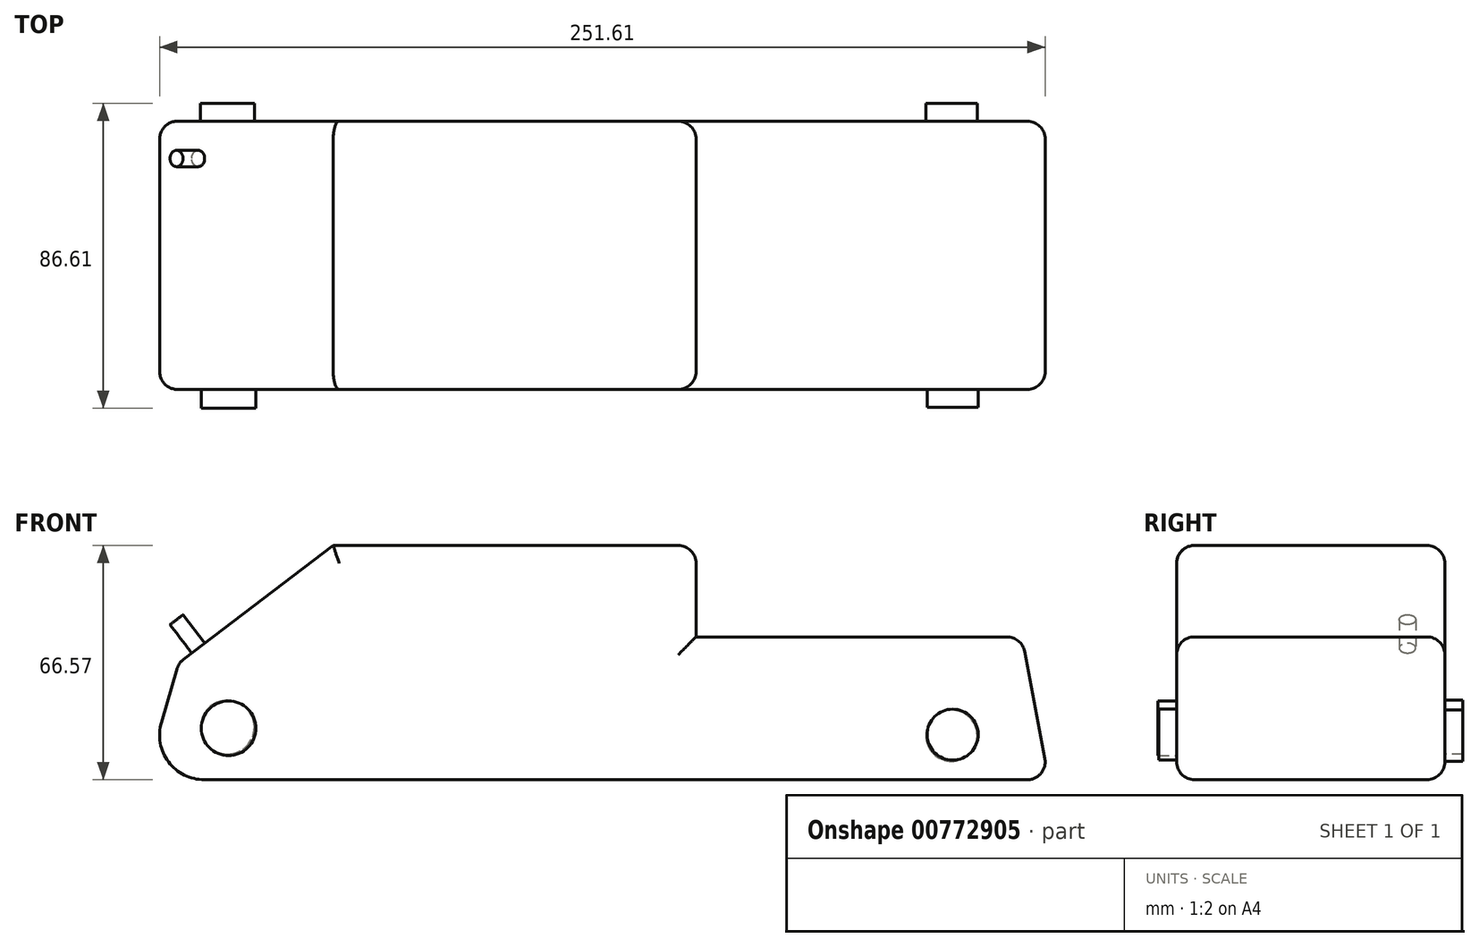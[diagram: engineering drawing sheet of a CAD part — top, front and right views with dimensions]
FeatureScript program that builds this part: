
annotation { "Feature Type Name" : "Feature", "Feature Type Description" : "" }
export const myFeature = defineFeature(function(context is Context, id is Id, definition is map)
    precondition{}
    {
        {
            var Q0;
            Q0=qCreatedBy(makeId("Front.planeOp"),FACE);
            var sketch = newSketch(context, id + "F0", { "sketchPlane" : qUnion([Q0])});
            skLineSegment(sketch, "E0", {"start": v(-130.55, -33.23) * mm, "end": v(126.37, -33.23) * mm});
            skLineSegment(sketch, "E1", {"start": v(126.37, -33.23) * mm, "end": v(118.66, 7.36) * mm});
            skLineSegment(sketch, "E2", {"start": v(118.66, 7.36) * mm, "end": v(26.12, 7.36) * mm});
            skLineSegment(sketch, "E3", {"start": v(26.12, 7.36) * mm, "end": v(26.12, 33.34) * mm});
            skLineSegment(sketch, "E4", {"start": v(26.12, 33.34) * mm, "end": v(-76.97, 33.34) * mm});
            skLineSegment(sketch, "E5", {"start": v(-76.97, 33.34) * mm, "end": v(-120.8, 0) * mm});
            skLineSegment(sketch, "E6", {"start": v(-120.8, 0) * mm, "end": v(-130.55, -33.23) * mm});
            skSolve(sketch);
        }
        {
            var Q0;
            Q0=makeQuery(id+"F0.imprint","IMPRINT",FACE,{"disambiguationData":[TD([[makeQuery(id+"F0.imprint","IMPRINT",EDGE,{"derivedFrom":sQuery(id+"F0.wireOp",EDGE,"E0")}),1.0]])]});
            extrude(context, id + "F1", {"entities" : qUnion([Q0]), "depth" : 76.2 * mm, "offsetDistance" : 25.4 * mm});
        }
        {
            var Q0;
            Q0=makeQuery(id+"F1.opExtrude","CAP_EDGE",EDGE,{"disambiguationData":[OSD([sQuery(id+"F0.wireOp",EDGE,"E6")])],"isStart":false});
            var Q1;
            Q1=makeQuery(id+"F1.opExtrude","CAP_EDGE",EDGE,{"disambiguationData":[OSD([sQuery(id+"F0.wireOp",EDGE,"E5")])],"isStart":false});
            var Q2;
            Q2=makeQuery(id+"F1.opExtrude","CAP_EDGE",EDGE,{"disambiguationData":[OSD([sQuery(id+"F0.wireOp",EDGE,"E4")])],"isStart":false});
            var Q3;
            Q3=makeQuery(id+"F1.opExtrude","CAP_EDGE",EDGE,{"disambiguationData":[OSD([sQuery(id+"F0.wireOp",EDGE,"E3")])],"isStart":false});
            var Q4;
            Q4=makeQuery(id+"F1.opExtrude","CAP_EDGE",EDGE,{"disambiguationData":[OSD([sQuery(id+"F0.wireOp",EDGE,"E3")])],"isStart":true});
            var Q5;
            Q5=makeQuery(id+"F1.opExtrude","SWEPT_EDGE",EDGE,{"disambiguationData":[OSD([sQuery(id+"F0.wireOp",EDGE,"E3"),sQuery(id+"F0.wireOp",EDGE,"E4")])]});
            var Q6;
            Q6=makeQuery(id+"F1.opExtrude","CAP_EDGE",EDGE,{"disambiguationData":[OSD([sQuery(id+"F0.wireOp",EDGE,"E5")])],"isStart":true});
            var Q7;
            Q7=makeQuery(id+"F1.opExtrude","CAP_EDGE",EDGE,{"disambiguationData":[OSD([sQuery(id+"F0.wireOp",EDGE,"E4")])],"isStart":true});
            var Q8;
            Q8=makeQuery(id+"F1.opExtrude","CAP_EDGE",EDGE,{"disambiguationData":[OSD([sQuery(id+"F0.wireOp",EDGE,"E6")])],"isStart":true});
            var Q9;
            Q9=makeQuery(id+"F1.opExtrude","CAP_EDGE",EDGE,{"disambiguationData":[OSD([sQuery(id+"F0.wireOp",EDGE,"E0")])],"isStart":true});
            var Q10;
            Q10=makeQuery(id+"F1.opExtrude","SWEPT_EDGE",EDGE,{"disambiguationData":[OSD([sQuery(id+"F0.wireOp",EDGE,"E5"),sQuery(id+"F0.wireOp",EDGE,"E6")])]});
            var Q11;
            Q11=makeQuery(id+"F1.opExtrude","CAP_EDGE",EDGE,{"disambiguationData":[OSD([sQuery(id+"F0.wireOp",EDGE,"E0")])],"isStart":false});
            var Q12;
            Q12=makeQuery(id+"F1.opExtrude","CAP_EDGE",EDGE,{"disambiguationData":[OSD([sQuery(id+"F0.wireOp",EDGE,"E2")])],"isStart":false});
            var Q13;
            Q13=makeQuery(id+"F1.opExtrude","SWEPT_EDGE",EDGE,{"disambiguationData":[OSD([sQuery(id+"F0.wireOp",EDGE,"E1"),sQuery(id+"F0.wireOp",EDGE,"E2")])]});
            var Q14;
            Q14=makeQuery(id+"F1.opExtrude","CAP_EDGE",EDGE,{"disambiguationData":[OSD([sQuery(id+"F0.wireOp",EDGE,"E1")])],"isStart":false});
            var Q15;
            Q15=makeQuery(id+"F1.opExtrude","SWEPT_EDGE",EDGE,{"disambiguationData":[OSD([sQuery(id+"F0.wireOp",EDGE,"E0"),sQuery(id+"F0.wireOp",EDGE,"E1")])]});
            var Q16;
            Q16=makeQuery(id+"F1.opExtrude","CAP_EDGE",EDGE,{"disambiguationData":[OSD([sQuery(id+"F0.wireOp",EDGE,"E1")])],"isStart":true});
            var Q17;
            Q17=makeQuery(id+"F1.opExtrude","CAP_EDGE",EDGE,{"disambiguationData":[OSD([sQuery(id+"F0.wireOp",EDGE,"E2")])],"isStart":true});
            fillet(context, id + "F2", {"entities" : qUnion([Q0, Q1, Q2, Q3, Q4, Q5, Q6, Q7, Q8, Q9, Q10, Q11, Q12, Q13, Q14, Q15, Q16, Q17]), "radius" : 5.08 * mm, "tangentPropagation" : true, "allowEdgeOverflow" : false});
        }
        {
            var Q0;
            Q0=makeQuery(id+"F1.opExtrude","SWEPT_EDGE",EDGE,{"disambiguationData":[OSD([sQuery(id+"F0.wireOp",EDGE,"E0"),sQuery(id+"F0.wireOp",EDGE,"E6")])]});
            fillet(context, id + "F3", {"entities" : qUnion([Q0]), "radius" : 12.7 * mm, "tangentPropagation" : true, "allowEdgeOverflow" : false});
        }
        {
            var Q0;
            Q0=makeQuery(id+"F1.opExtrude","CAP_FACE",FACE,{"disambiguationData":[OSD([sQuery(id+"F0.wireOp",EDGE,"E0"),sQuery(id+"F0.wireOp",EDGE,"E1"),sQuery(id+"F0.wireOp",EDGE,"E2"),sQuery(id+"F0.wireOp",EDGE,"E3"),sQuery(id+"F0.wireOp",EDGE,"E4"),sQuery(id+"F0.wireOp",EDGE,"E5"),sQuery(id+"F0.wireOp",EDGE,"E6")])],"isStart":false});
            var sketch = newSketch(context, id + "F4", { "sketchPlane" : qUnion([Q0])});
            skCircle(sketch, "E7", {"center": v(-106.68, -18.61) * mm, "radius": 7.75 * mm});
            skSolve(sketch);
        }
        {
            var Q0;
            Q0=makeQuery(id+"F4.imprint","IMPRINT",FACE,{"disambiguationData":[TD([[makeQuery(id+"F4.imprint","IMPRINT",EDGE,{"derivedFrom":sQuery(id+"F4.wireOp",EDGE,"E7")}),1.0]])]});
            extrude(context, id + "F5", {"entities" : qUnion([Q0]), "operationType" : NewBodyOperationType.ADD, "depth" : 0.25 * mm, "offsetDistance" : 25.4 * mm});
        }
        {
            var Q0;
            Q0=makeQuery(id+"F5.opExtrude","CAP_FACE",FACE,{"disambiguationData":[OSD([sQuery(id+"F4.wireOp",EDGE,"E7")])],"isStart":false});
            extrude(context, id + "F6", {"entities" : qUnion([Q0]), "operationType" : NewBodyOperationType.ADD, "depth" : 5.08 * mm, "offsetDistance" : 25.4 * mm});
        }
        {
            var Q0;
            Q0=makeQuery(id+"F1.opExtrude","CAP_FACE",FACE,{"disambiguationData":[OSD([sQuery(id+"F0.wireOp",EDGE,"E0"),sQuery(id+"F0.wireOp",EDGE,"E1"),sQuery(id+"F0.wireOp",EDGE,"E2"),sQuery(id+"F0.wireOp",EDGE,"E3"),sQuery(id+"F0.wireOp",EDGE,"E4"),sQuery(id+"F0.wireOp",EDGE,"E5"),sQuery(id+"F0.wireOp",EDGE,"E6")])],"isStart":true});
            var sketch = newSketch(context, id + "F7", { "sketchPlane" : qUnion([Q0])});
            skCircle(sketch, "E8", {"center": v(107.01, -18.29) * mm, "radius": 7.64 * mm});
            skSolve(sketch);
        }
        {
            var Q0;
            Q0=makeQuery(id+"F7.imprint","IMPRINT",FACE,{"disambiguationData":[TD([[makeQuery(id+"F7.imprint","IMPRINT",EDGE,{"derivedFrom":sQuery(id+"F7.wireOp",EDGE,"E8")}),1.0]])]});
            extrude(context, id + "F8", {"entities" : qUnion([Q0]), "operationType" : NewBodyOperationType.ADD, "depth" : 5.08 * mm, "offsetDistance" : 25.4 * mm});
        }
        {
            var Q0;
            Q0=makeQuery(id+"F4.imprint","IMPRINT",FACE,{"disambiguationData":[TD([[makeQuery(id+"F4.imprint","IMPRINT",EDGE,{"derivedFrom":sQuery(id+"F4.wireOp",EDGE,"E7")}),-1.0]])]});
            var sketch = newSketch(context, id + "F9", { "sketchPlane" : qUnion([Q0])});
            skCircle(sketch, "E9", {"center": v(99.03, -20.42) * mm, "radius": 7.25 * mm});
            skSolve(sketch);
        }
        {
            var Q0;
            Q0=makeQuery(id+"F1.opExtrude","CAP_FACE",FACE,{"disambiguationData":[OSD([sQuery(id+"F0.wireOp",EDGE,"E0"),sQuery(id+"F0.wireOp",EDGE,"E1"),sQuery(id+"F0.wireOp",EDGE,"E2"),sQuery(id+"F0.wireOp",EDGE,"E3"),sQuery(id+"F0.wireOp",EDGE,"E4"),sQuery(id+"F0.wireOp",EDGE,"E5"),sQuery(id+"F0.wireOp",EDGE,"E6")])],"isStart":true});
            var sketch = newSketch(context, id + "F10", { "sketchPlane" : qUnion([Q0])});
            skCircle(sketch, "E10", {"center": v(-98.73, -20.73) * mm, "radius": 7.27 * mm});
            skSolve(sketch);
        }
        {
            var Q0;
            Q0=makeQuery(id+"F10.imprint","IMPRINT",FACE,{"disambiguationData":[TD([[makeQuery(id+"F10.imprint","IMPRINT",EDGE,{"derivedFrom":sQuery(id+"F10.wireOp",EDGE,"E10")}),1.0]])]});
            extrude(context, id + "F11", {"entities" : qUnion([Q0]), "operationType" : NewBodyOperationType.ADD, "depth" : 5.08 * mm, "offsetDistance" : 25.4 * mm});
        }
        {
            var Q0;
            Q0=makeQuery(id+"F9.imprint","IMPRINT",FACE,{"disambiguationData":[TD([[makeQuery(id+"F9.imprint","IMPRINT",EDGE,{"derivedFrom":sQuery(id+"F9.wireOp",EDGE,"E9")}),1.0]])]});
            extrude(context, id + "F12", {"entities" : qUnion([Q0]), "operationType" : NewBodyOperationType.ADD, "depth" : 5.08 * mm, "offsetDistance" : 25.4 * mm});
        }
        {
            var Q0;
            Q0=makeQuery(id+"F1.opExtrude","SWEPT_FACE",FACE,{"disambiguationData":[OSD([sQuery(id+"F0.wireOp",EDGE,"E5")])]});
            var sketch = newSketch(context, id + "F13", { "sketchPlane" : qUnion([Q0])});
            skCircle(sketch, "E11", {"center": v(-89.27, -10.6) * mm, "radius": 2.32 * mm});
            skSolve(sketch);
        }
        {
            var Q0;
            Q0=makeQuery(id+"F13.imprint","IMPRINT",FACE,{"disambiguationData":[TD([[makeQuery(id+"F13.imprint","IMPRINT",EDGE,{"derivedFrom":sQuery(id+"F13.wireOp",EDGE,"E11")}),1.0]])]});
            extrude(context, id + "F14", {"entities" : qUnion([Q0]), "operationType" : NewBodyOperationType.ADD, "depth" : 10.16 * mm, "offsetDistance" : 25.4 * mm});
        }
        {
            var Q0;
            Q0=makeQuery(id+"F4.imprint","IMPRINT",FACE,{"disambiguationData":[TD([[makeQuery(id+"F4.imprint","IMPRINT",EDGE,{"derivedFrom":sQuery(id+"F4.wireOp",EDGE,"E7")}),-1.0]])]});
            var sketch = newSketch(context, id + "F15", { "sketchPlane" : qUnion([Q0])});
            skLineSegment(sketch, "E12", {"start": v(-22.44, 27.91) * mm, "end": v(-22.44, -27.58) * mm});
            skLineSegment(sketch, "E13", {"start": v(-22.44, 3.94) * mm, "end": v(20.58, 3.94) * mm});
            skLineSegment(sketch, "E14", {"start": v(20.58, 3.94) * mm, "end": v(20.58, -27.91) * mm});
            skSolve(sketch);
        }
        {
            var Q0;
            Q0=sQuery(id+"F15.wireOp",EDGE,"E12");
            extrude(context, id + "F16", {"bodyType" : ToolBodyType.SURFACE, "surfaceEntities" : qUnion([Q0]), "depth" : 2.54 * mm, "offsetDistance" : 25.4 * mm});
        }
        {
            var Q0;
            Q0=sQuery(id+"F15.wireOp",EDGE,"E13");
            extrude(context, id + "F17", {"bodyType" : ToolBodyType.SURFACE, "surfaceEntities" : qUnion([Q0]), "depth" : 2.54 * mm, "offsetDistance" : 25.4 * mm});
        }
        {
            var Q0;
            Q0=sQuery(id+"F15.wireOp",EDGE,"E14");
            extrude(context, id + "F18", {"bodyType" : ToolBodyType.SURFACE, "surfaceEntities" : qUnion([Q0]), "depth" : 2.54 * mm, "offsetDistance" : 25.4 * mm});
        }
        {
            var Q0;
            Q0=makeQuery(id+"F4.imprint","IMPRINT",FACE,{"disambiguationData":[TD([[makeQuery(id+"F4.imprint","IMPRINT",EDGE,{"derivedFrom":sQuery(id+"F4.wireOp",EDGE,"E7")}),-1.0]])]});
            var sketch = newSketch(context, id + "F19", { "sketchPlane" : qUnion([Q0])});
            skLineSegment(sketch, "E15", {"start": v(-22.48, 28.53) * mm, "end": v(-17.07, 28.53) * mm});
            skLineSegment(sketch, "E16", {"start": v(-17.07, 28.53) * mm, "end": v(-17.07, -27.18) * mm});
            skLineSegment(sketch, "E17", {"start": v(-17.07, -27.18) * mm, "end": v(14.66, -27.18) * mm});
            skLineSegment(sketch, "E18", {"start": v(14.66, -27.18) * mm, "end": v(14.66, 3.55) * mm});
            skLineSegment(sketch, "E19", {"start": v(14.66, 3.55) * mm, "end": v(-17.07, 3.55) * mm});
            skSolve(sketch);
        }
        {
            var Q0;
            Q0=sQuery(id+"F19.wireOp",EDGE,"E16");
            extrude(context, id + "F20", {"bodyType" : ToolBodyType.SURFACE, "surfaceEntities" : qUnion([Q0]), "depth" : 2.54 * mm, "offsetDistance" : 25.4 * mm});
        }
    });
